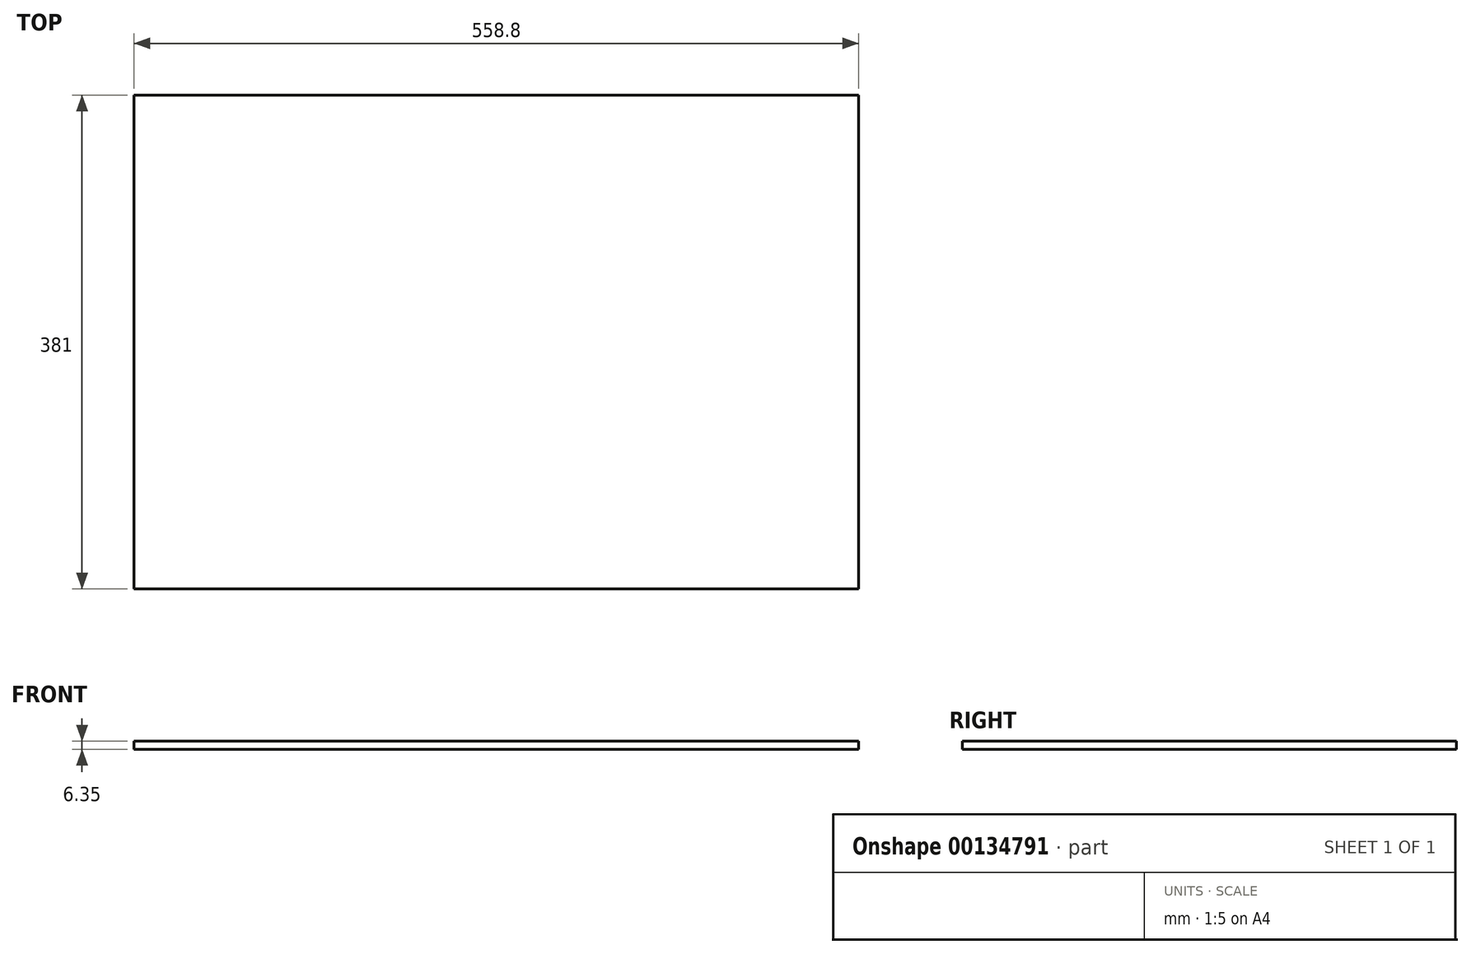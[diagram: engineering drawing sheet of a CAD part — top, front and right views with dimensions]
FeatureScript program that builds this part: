
annotation { "Feature Type Name" : "Feature", "Feature Type Description" : "" }
export const myFeature = defineFeature(function(context is Context, id is Id, definition is map)
    precondition{}
    {
        {
            var Q0;
            Q0=qCreatedBy(makeId("Top.planeOp"),FACE);
            var sketch = newSketch(context, id + "F0", { "sketchPlane" : qUnion([Q0])});
            skLineSegment(sketch, "E0.bottom", {"start": v(279.4, 190.5) * mm, "end": v(-279.4, 190.5) * mm});
            skLineSegment(sketch, "E0.top", {"start": v(279.4, -190.5) * mm, "end": v(-279.4, -190.5) * mm});
            skLineSegment(sketch, "E0.left", {"start": v(279.4, 190.5) * mm, "end": v(279.4, -190.5) * mm});
            skLineSegment(sketch, "E0.right", {"start": v(-279.4, 190.5) * mm, "end": v(-279.4, -190.5) * mm});
            skPoint(sketch, "E0.middle", {"position": v(0, 0) * mm});
            skSolve(sketch);
        }
        {
            var Q0;
            Q0=makeQuery(id+"F0.imprint","IMPRINT",FACE,{"disambiguationData":[TD([[makeQuery(id+"F0.imprint","IMPRINT",EDGE,{"derivedFrom":sQuery(id+"F0.wireOp",EDGE,"E0.bottom")}),1.0]])]});
            extrude(context, id + "F1", {"entities" : qUnion([Q0]), "depth" : 6.35 * mm});
        }
    });
